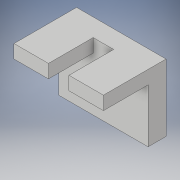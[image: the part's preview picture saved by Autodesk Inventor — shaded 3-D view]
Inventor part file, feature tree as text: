
AUTODESK INVENTOR PART (.ipt)
format: ipt  version: 2017 (Build 210142000, 142)  size: 103,936 bytes
history: native  units: in
note: dims shown in document units (in); Inventor stores cm internally (conversion verified against a paired STEP export)
features: extrude x2, sketch x2
ambient origin geometry x8: Origin, YZ Plane, XZ Plane, XY Plane, X Axis, Y Axis, Z Axis, Center Point
bodies: Solid1 (feature_tree)
feature tree (4):
  extrude  "Extrusion1"  Depth=0.75in
  extrude  "Extrusion2"  Depth=0.385in
  sketch  "Sketch1"  dims[d0=1.0in d1=0.75in]
  sketch  "Sketch2"  dims[d2=0.2in d3=0.0in d4=0.385in d5=0.15in d6=0.385in d7=0.5in d8=0.0in]
